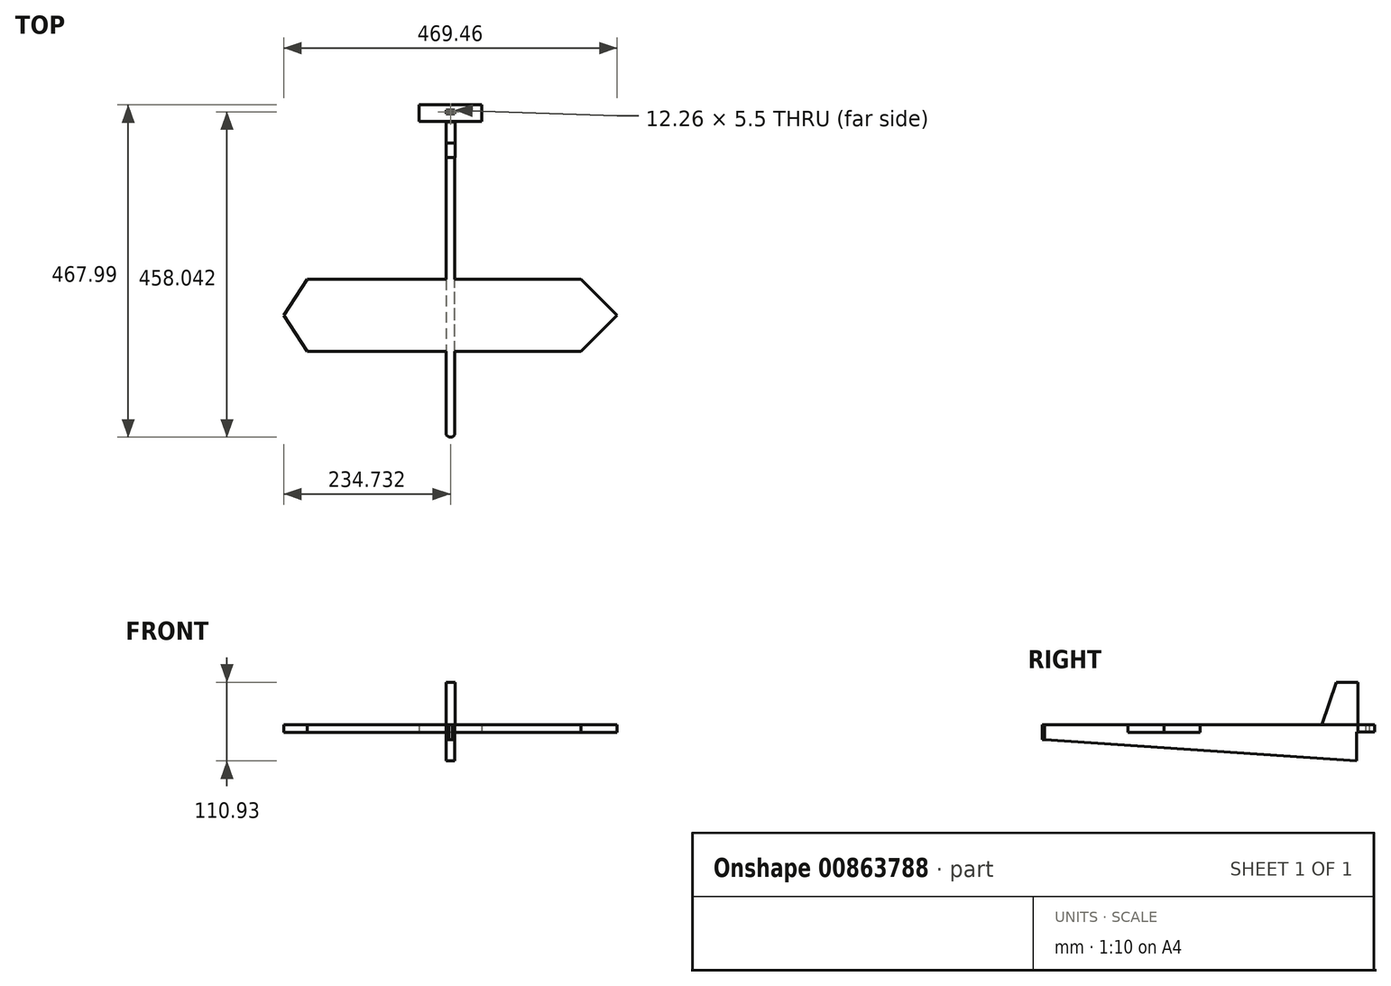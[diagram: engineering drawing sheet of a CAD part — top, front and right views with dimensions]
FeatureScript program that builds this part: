
annotation { "Feature Type Name" : "Feature", "Feature Type Description" : "" }
export const myFeature = defineFeature(function(context is Context, id is Id, definition is map)
    precondition{}
    {
        {
            var Q0;
            Q0=qCreatedBy(makeId("Top.planeOp"),FACE);
            var sketch = newSketch(context, id + "F0", { "sketchPlane" : qUnion([Q0])});
            skLineSegment(sketch, "E0", {"start": v(0, 404.58) * mm, "end": v(0, -52.62) * mm});
            skLineSegment(sketch, "E1", {"start": v(0, -52.62) * mm, "end": v(3.6, -56.2) * mm});
            skLineSegment(sketch, "E2", {"start": v(3.6, -56.2) * mm, "end": v(8.67, -56.2) * mm});
            skLineSegment(sketch, "E3", {"start": v(8.67, -56.2) * mm, "end": v(12.26, -52.62) * mm});
            skLineSegment(sketch, "E4", {"start": v(12.26, -52.62) * mm, "end": v(12.26, 403.42) * mm});
            skLineSegment(sketch, "E5", {"start": v(0, 404.58) * mm, "end": v(12.26, 404.58) * mm});
            skLineSegment(sketch, "E6", {"start": v(12.26, 404.58) * mm, "end": v(12.26, 403.42) * mm});
            skLineSegment(sketch, "E7", {"start": v(12.26, 64.6) * mm, "end": v(240.86, 64.6) * mm});
            skLineSegment(sketch, "E8", {"start": v(240.86, 64.6) * mm, "end": v(240.86, 166.2) * mm});
            skLineSegment(sketch, "E9", {"start": v(240.86, 166.2) * mm, "end": v(12.26, 166.2) * mm});
            skLineSegment(sketch, "E10", {"start": v(12.26, 166.2) * mm, "end": v(0, 166.2) * mm});
            skLineSegment(sketch, "E11", {"start": v(0, 166.2) * mm, "end": v(-228.6, 166.2) * mm});
            skLineSegment(sketch, "E12", {"start": v(-228.6, 166.2) * mm, "end": v(-228.6, 64.6) * mm});
            skLineSegment(sketch, "E13", {"start": v(-228.6, 64.6) * mm, "end": v(12.26, 64.6) * mm});
            skLineSegment(sketch, "E14", {"start": v(12.26, 388.54) * mm, "end": v(37.66, 388.54) * mm});
            skLineSegment(sketch, "E15", {"start": v(37.66, 388.54) * mm, "end": v(12.26, 388.54) * mm});
            skLineSegment(sketch, "E16", {"start": v(0, 388.54) * mm, "end": v(-25.4, 388.54) * mm});
            skLineSegment(sketch, "E17", {"start": v(-25.4, 388.54) * mm, "end": v(-38.1, 388.54) * mm});
            skLineSegment(sketch, "E18", {"start": v(-38.1, 388.54) * mm, "end": v(37.66, 388.54) * mm});
            skLineSegment(sketch, "E19", {"start": v(37.66, 388.54) * mm, "end": v(50.36, 388.54) * mm});
            skLineSegment(sketch, "E20", {"start": v(50.36, 388.54) * mm, "end": v(50.36, 399.08) * mm});
            skLineSegment(sketch, "E21", {"start": v(12.26, 399.08) * mm, "end": v(0, 399.08) * mm});
            skLineSegment(sketch, "E22", {"start": v(-38.1, 399.08) * mm, "end": v(-38.1, 388.54) * mm});
            skLineSegment(sketch, "E23", {"start": v(50.36, 399.08) * mm, "end": v(50.36, 411.78) * mm});
            skLineSegment(sketch, "E24", {"start": v(-38.1, 399.08) * mm, "end": v(-38.1, 411.78) * mm});
            skLineSegment(sketch, "E25", {"start": v(-38.1, 411.78) * mm, "end": v(50.36, 411.78) * mm});
            skSolve(sketch);
        }
        {
            var Q0;
            Q0 = qSketchRegion(id + "F0", true);
            extrude(context, id + "F1", {"entities" : qUnion([Q0]), "depth" : 50.8 * mm, "offsetDistance" : 25.4 * mm});
        }
        {
            var Q0;
            Q0=makeQuery(id+"F1.opExtrude","SWEPT_FACE",FACE,{"disambiguationData":[OSD([sQuery(id+"F0.wireOp",EDGE,"E8")])]});
            var sketch = newSketch(context, id + "F2", { "sketchPlane" : qUnion([Q0])});
            skLineSegment(sketch, "E26", {"start": v(64.6, 40.28) * mm, "end": v(166.2, 40.28) * mm});
            skLineSegment(sketch, "E27", {"start": v(166.2, 40.28) * mm, "end": v(166.2, 50.8) * mm});
            skLineSegment(sketch, "E28", {"start": v(166.2, 50.8) * mm, "end": v(166.2, 40.28) * mm});
            skLineSegment(sketch, "E29", {"start": v(166.2, 40.28) * mm, "end": v(166.2, 0) * mm});
            skLineSegment(sketch, "E30", {"start": v(166.2, 0) * mm, "end": v(64.6, 0) * mm});
            skLineSegment(sketch, "E31", {"start": v(64.6, 0) * mm, "end": v(64.6, 40.28) * mm});
            skSolve(sketch);
        }
        {
            var Q0;
            Q0 = qSketchRegion(id + "F2", true);
            extrude(context, id + "F3", {"entities" : qUnion([Q0]), "operationType" : NewBodyOperationType.REMOVE, "oppositeDirection" : true, "depth" : 228.6 * mm, "offsetDistance" : 25.4 * mm});
        }
        {
            var Q0;
            Q0=makeQuery(id+"F1.opExtrude","SWEPT_FACE",FACE,{"disambiguationData":[OSD([sQuery(id+"F0.wireOp",EDGE,"E12")])]});
            var sketch = newSketch(context, id + "F4", { "sketchPlane" : qUnion([Q0])});
            skLineSegment(sketch, "E32", {"start": v(-166.2, 50.8) * mm, "end": v(-166.2, 40.28) * mm});
            skLineSegment(sketch, "E33", {"start": v(-166.2, 40.28) * mm, "end": v(-64.6, 40.28) * mm});
            skLineSegment(sketch, "E34", {"start": v(-64.6, 40.28) * mm, "end": v(-64.6, 0) * mm});
            skLineSegment(sketch, "E35", {"start": v(-64.6, 0) * mm, "end": v(-166.2, 0) * mm});
            skLineSegment(sketch, "E36", {"start": v(-166.2, 0) * mm, "end": v(-166.42, 40.86) * mm});
            skLineSegment(sketch, "E37", {"start": v(-166.42, 40.86) * mm, "end": v(-64.6, 40.28) * mm});
            skLineSegment(sketch, "E38", {"start": v(-64.6, 0) * mm, "end": v(-64.6, 40.28) * mm});
            skSolve(sketch);
        }
        {
            var Q0;
            Q0 = qSketchRegion(id + "F4", true);
            extrude(context, id + "F5", {"entities" : qUnion([Q0]), "operationType" : NewBodyOperationType.REMOVE, "oppositeDirection" : true, "depth" : 228.6 * mm, "offsetDistance" : 25.4 * mm});
        }
        {
            var Q0;
            {var subQ0=sQuery(id+"F0.wireOp",EDGE,"E0");Q0=makeQuery(id+"FdQB89tJsIS8Kwt_1.boolean.opBoolean","MERGE",FACE,{"derivedFrom":[makeQuery(id+"F1.opExtrude","SWEPT_FACE",FACE,{"disambiguationData":[OSD([subQ0]),TDD([makeQuery(id+"F0.imprint","IMPRINT",EDGE,{"disambiguationData":[TD([[makeQuery(id+"F0.imprint","INTERSECT",VERTEX,{"derivedFrom":[subQ0,sQuery(id+"F0.wireOp",EDGE,"E5")]}),-1.0]])],"derivedFrom":subQ0})])]}),makeQuery(id+"F5.boolean.opBoolean","MERGE",FACE,{"derivedFrom":[makeQuery(id+"F1.opExtrude","SWEPT_FACE",FACE,{"disambiguationData":[OSD([subQ0]),TDD([makeQuery(id+"F0.imprint","IMPRINT",EDGE,{"disambiguationData":[TD([[makeQuery(id+"F0.imprint","INTERSECT",VERTEX,{"derivedFrom":[subQ0,sQuery(id+"F0.wireOp",EDGE,"E18")]}),-1.0]])],"derivedFrom":subQ0})])]}),makeQuery(id+"F1.opExtrude","SWEPT_FACE",FACE,{"disambiguationData":[OSD([subQ0]),TDD([makeQuery(id+"F0.imprint","IMPRINT",EDGE,{"disambiguationData":[TD([[makeQuery(id+"F0.imprint","INTERSECT",VERTEX,{"derivedFrom":[subQ0,sQuery(id+"F0.wireOp",EDGE,"E1")]}),1.0]])],"derivedFrom":subQ0})])]}),makeQuery(id+"F5.opExtrude","CAP_FACE",FACE,{"disambiguationData":[OSD([sQuery(id+"F4.wireOp",EDGE,"E36"),sQuery(id+"F4.wireOp",EDGE,"E37"),sQuery(id+"F4.wireOp",EDGE,"E38"),sQuery(id+"F4.wireOp",EDGE,"E35")])],"isStart":false})]}),makeQuery(id+"FdQB89tJsIS8Kwt_1.opExtrude","SWEPT_FACE",FACE,{"disambiguationData":[OSD([sQuery(id+"FIC4QPpxlJvvk01_1.wireOp",EDGE,"bgQTwSuV-lAzQ-jPFc-NSy7-3OVJcPBx1S6P")])]})]});}
            var sketch = newSketch(context, id + "F6", { "sketchPlane" : qUnion([Q0])});
            skLineSegment(sketch, "E39", {"start": v(865.4, 33.14) * mm, "end": v(404.58, 0) * mm});
            skLineSegment(sketch, "E40", {"start": v(56.47, 0) * mm, "end": v(404.58, 0) * mm});
            skLineSegment(sketch, "E41", {"start": v(56.47, 0) * mm, "end": v(865.4, 33.14) * mm});
            skSolve(sketch);
        }
        {
            var Q0;
            Q0 = qSketchRegion(id + "F6", true);
            extrude(context, id + "F7", {"entities" : qUnion([Q0]), "operationType" : NewBodyOperationType.REMOVE, "oppositeDirection" : true, "depth" : 25.4 * mm, "offsetDistance" : 25.4 * mm});
        }
        {
            var Q0;
            Q0=makeQuery(id+"F1.opExtrude","SWEPT_FACE",FACE,{"disambiguationData":[OSD([sQuery(id+"F0.wireOp",EDGE,"E25")])]});
            var sketch = newSketch(context, id + "F8", { "sketchPlane" : qUnion([Q0])});
            skLineSegment(sketch, "E42", {"start": v(-50.36, 40.75) * mm, "end": v(38.1, 40.75) * mm});
            skLineSegment(sketch, "E43", {"start": v(38.1, 40.75) * mm, "end": v(38.1, 0) * mm});
            skLineSegment(sketch, "E44", {"start": v(38.1, 0) * mm, "end": v(-50.36, 0) * mm});
            skLineSegment(sketch, "E45", {"start": v(-50.36, 0) * mm, "end": v(-50.36, 40.75) * mm});
            skSolve(sketch);
        }
        {
            var Q0;
            Q0 = qSketchRegion(id + "F8", true);
            extrude(context, id + "F9", {"entities" : qUnion([Q0]), "operationType" : NewBodyOperationType.REMOVE, "oppositeDirection" : true, "depth" : 25.4 * mm, "offsetDistance" : 25.4 * mm});
        }
        {
            var Q0;
            {var subQ0=sQuery(id+"F0.wireOp",EDGE,"E0");Q0=makeQuery(id+"F7.boolean.opBoolean","MERGE",FACE,{"derivedFrom":[makeQuery(id+"F5.boolean.opBoolean","MERGE",FACE,{"derivedFrom":[makeQuery(id+"F1.opExtrude","SWEPT_FACE",FACE,{"disambiguationData":[OSD([subQ0]),TDD([makeQuery(id+"F0.imprint","IMPRINT",EDGE,{"disambiguationData":[TD([[makeQuery(id+"F0.imprint","INTERSECT",VERTEX,{"derivedFrom":[subQ0,sQuery(id+"F0.wireOp",EDGE,"E18")]}),-1.0]])],"derivedFrom":subQ0})])]}),makeQuery(id+"F1.opExtrude","SWEPT_FACE",FACE,{"disambiguationData":[OSD([subQ0]),TDD([makeQuery(id+"F0.imprint","IMPRINT",EDGE,{"disambiguationData":[TD([[makeQuery(id+"F0.imprint","INTERSECT",VERTEX,{"derivedFrom":[subQ0,sQuery(id+"F0.wireOp",EDGE,"E1")]}),1.0]])],"derivedFrom":subQ0})])]}),makeQuery(id+"F5.opExtrude","CAP_FACE",FACE,{"disambiguationData":[OSD([sQuery(id+"F4.wireOp",EDGE,"E36"),sQuery(id+"F4.wireOp",EDGE,"E37"),sQuery(id+"F4.wireOp",EDGE,"E38"),sQuery(id+"F4.wireOp",EDGE,"E35")])],"isStart":false})]}),makeQuery(id+"F7.opExtrude","CAP_FACE",FACE,{"disambiguationData":[OSD([sQuery(id+"F6.wireOp",EDGE,"E39"),sQuery(id+"F6.wireOp",EDGE,"E40"),sQuery(id+"F6.wireOp",EDGE,"E41")])],"isStart":true})]});}
            var sketch = newSketch(context, id + "F10", { "sketchPlane" : qUnion([Q0])});
            skLineSegment(sketch, "E46", {"start": v(-309.16, 50.8) * mm, "end": v(-337.9, 50.8) * mm});
            skLineSegment(sketch, "E47", {"start": v(-337.9, 50.8) * mm, "end": v(-358.33, 110.93) * mm});
            skLineSegment(sketch, "E48", {"start": v(-358.33, 110.93) * mm, "end": v(-388.54, 110.93) * mm});
            skLineSegment(sketch, "E49", {"start": v(-388.54, 110.93) * mm, "end": v(-388.54, 50.8) * mm});
            skLineSegment(sketch, "E50", {"start": v(-388.54, 50.8) * mm, "end": v(-388.54, 72.19) * mm});
            skPoint(sketch, "E51.end.orphan", {"position": v(-388.54, 53.46) * mm});
            skLineSegment(sketch, "E52", {"start": v(-388.54, 50.8) * mm, "end": v(-337.9, 50.8) * mm});
            skSolve(sketch);
        }
        {
            var Q0;
            Q0 = qSketchRegion(id + "F10", true);
            extrude(context, id + "F11", {"entities" : qUnion([Q0]), "oppositeDirection" : true, "depth" : 12.7 * mm, "offsetDistance" : 25.4 * mm});
        }
        {
            var Q0;
            {var subQ0=sQuery(id+"F0.wireOp",EDGE,"E4");Q0=makeQuery(id+"F3.boolean.opBoolean","MERGE",FACE,{"derivedFrom":[makeQuery(id+"F1.opExtrude","SWEPT_FACE",FACE,{"disambiguationData":[OSD([subQ0]),TDD([makeQuery(id+"F0.imprint","IMPRINT",EDGE,{"disambiguationData":[TD([[makeQuery(id+"F0.imprint","INTERSECT",VERTEX,{"derivedFrom":[sQuery(id+"F0.wireOp",EDGE,"E3"),subQ0]}),-1.0]])],"derivedFrom":subQ0})])]}),makeQuery(id+"F1.opExtrude","SWEPT_FACE",FACE,{"disambiguationData":[OSD([subQ0]),TDD([makeQuery(id+"F0.imprint","IMPRINT",EDGE,{"disambiguationData":[TD([[makeQuery(id+"F0.imprint","INTERSECT",VERTEX,{"derivedFrom":[subQ0,sQuery(id+"F0.wireOp",EDGE,"E18")]}),1.0]])],"derivedFrom":subQ0})])]}),makeQuery(id+"F3.opExtrude","CAP_FACE",FACE,{"disambiguationData":[OSD([sQuery(id+"F2.wireOp",EDGE,"E26"),sQuery(id+"F2.wireOp",EDGE,"E29"),sQuery(id+"F2.wireOp",EDGE,"E30"),sQuery(id+"F2.wireOp",EDGE,"E31")])],"isStart":false})]});}
            var sketch = newSketch(context, id + "F12", { "sketchPlane" : qUnion([Q0])});
            skLineSegment(sketch, "E53", {"start": v(-56.54, 30.1) * mm, "end": v(386.38, 0) * mm});
            skLineSegment(sketch, "E54", {"start": v(386.38, 0) * mm, "end": v(-56.54, 0) * mm});
            skLineSegment(sketch, "E55", {"start": v(-56.54, 0) * mm, "end": v(-56.54, 30.1) * mm});
            skSolve(sketch);
        }
        {
            var Q0;
            Q0 = qSketchRegion(id + "F12", true);
            extrude(context, id + "F13", {"entities" : qUnion([Q0]), "operationType" : NewBodyOperationType.REMOVE, "oppositeDirection" : true, "depth" : 25.4 * mm, "offsetDistance" : 25.4 * mm});
        }
        {
            var Q0;
            Q0=makeQuery(id+"F1.opExtrude","CAP_FACE",FACE,{"disambiguationData":[OSD([sQuery(id+"F0.wireOp",EDGE,"E0"),sQuery(id+"F0.wireOp",EDGE,"E1"),sQuery(id+"F0.wireOp",EDGE,"E2"),sQuery(id+"F0.wireOp",EDGE,"E3"),sQuery(id+"F0.wireOp",EDGE,"E4"),sQuery(id+"F0.wireOp",EDGE,"E5"),sQuery(id+"F0.wireOp",EDGE,"E6"),sQuery(id+"F0.wireOp",EDGE,"E7"),sQuery(id+"F0.wireOp",EDGE,"E8"),sQuery(id+"F0.wireOp",EDGE,"E9"),sQuery(id+"F0.wireOp",EDGE,"E11"),sQuery(id+"F0.wireOp",EDGE,"E12"),sQuery(id+"F0.wireOp",EDGE,"E13"),sQuery(id+"F0.wireOp",EDGE,"E18"),sQuery(id+"F0.wireOp",EDGE,"E19"),sQuery(id+"F0.wireOp",EDGE,"E20"),sQuery(id+"F0.wireOp",EDGE,"E21"),sQuery(id+"F0.wireOp",EDGE,"E22"),sQuery(id+"F0.wireOp",EDGE,"E23"),sQuery(id+"F0.wireOp",EDGE,"E24"),sQuery(id+"F0.wireOp",EDGE,"E25")])],"isStart":false});
            var sketch = newSketch(context, id + "F14", { "sketchPlane" : qUnion([Q0])});
            skLineSegment(sketch, "E56", {"start": v(0, 166.2) * mm, "end": v(-17.78, 166.2) * mm});
            skLineSegment(sketch, "E57", {"start": v(-17.78, 166.2) * mm, "end": v(-195.58, 166.2) * mm});
            skLineSegment(sketch, "E58", {"start": v(-195.58, 166.2) * mm, "end": v(-228.6, 115.4) * mm});
            skLineSegment(sketch, "E59", {"start": v(0, 64.6) * mm, "end": v(-17.78, 64.6) * mm});
            skLineSegment(sketch, "E60", {"start": v(-17.78, 64.6) * mm, "end": v(-195.58, 64.6) * mm});
            skLineSegment(sketch, "E61", {"start": v(-195.58, 64.6) * mm, "end": v(-228.6, 115.4) * mm});
            skLineSegment(sketch, "E62", {"start": v(-195.58, 166.2) * mm, "end": v(-228.6, 166.2) * mm});
            skLineSegment(sketch, "E63", {"start": v(-228.6, 166.2) * mm, "end": v(-228.6, 64.6) * mm});
            skLineSegment(sketch, "E64", {"start": v(-228.6, 64.6) * mm, "end": v(-195.58, 64.6) * mm});
            skSolve(sketch);
        }
        {
            var Q0;
            Q0 = qSketchRegion(id + "F14", true);
            extrude(context, id + "F15", {"entities" : qUnion([Q0]), "operationType" : NewBodyOperationType.REMOVE, "oppositeDirection" : true, "depth" : 25.4 * mm, "offsetDistance" : 25.4 * mm});
        }
        {
            var Q0;
            Q0=makeQuery(id+"F1.opExtrude","CAP_FACE",FACE,{"disambiguationData":[OSD([sQuery(id+"F0.wireOp",EDGE,"E0"),sQuery(id+"F0.wireOp",EDGE,"E1"),sQuery(id+"F0.wireOp",EDGE,"E2"),sQuery(id+"F0.wireOp",EDGE,"E3"),sQuery(id+"F0.wireOp",EDGE,"E4"),sQuery(id+"F0.wireOp",EDGE,"E5"),sQuery(id+"F0.wireOp",EDGE,"E6"),sQuery(id+"F0.wireOp",EDGE,"E7"),sQuery(id+"F0.wireOp",EDGE,"E8"),sQuery(id+"F0.wireOp",EDGE,"E9"),sQuery(id+"F0.wireOp",EDGE,"E11"),sQuery(id+"F0.wireOp",EDGE,"E12"),sQuery(id+"F0.wireOp",EDGE,"E13"),sQuery(id+"F0.wireOp",EDGE,"E18"),sQuery(id+"F0.wireOp",EDGE,"E19"),sQuery(id+"F0.wireOp",EDGE,"E20"),sQuery(id+"F0.wireOp",EDGE,"E21"),sQuery(id+"F0.wireOp",EDGE,"E22"),sQuery(id+"F0.wireOp",EDGE,"E23"),sQuery(id+"F0.wireOp",EDGE,"E24"),sQuery(id+"F0.wireOp",EDGE,"E25")])],"isStart":false});
            var sketch = newSketch(context, id + "F16", { "sketchPlane" : qUnion([Q0])});
            skLineSegment(sketch, "E65", {"start": v(12.26, 166.2) * mm, "end": v(190.06, 166.2) * mm});
            skLineSegment(sketch, "E66", {"start": v(190.06, 166.2) * mm, "end": v(240.86, 115.4) * mm});
            skLineSegment(sketch, "E67", {"start": v(12.26, 64.6) * mm, "end": v(190.06, 64.6) * mm});
            skLineSegment(sketch, "E68", {"start": v(190.06, 64.6) * mm, "end": v(240.86, 115.4) * mm});
            skLineSegment(sketch, "E69", {"start": v(190.06, 166.2) * mm, "end": v(240.86, 166.2) * mm});
            skLineSegment(sketch, "E70", {"start": v(240.86, 166.2) * mm, "end": v(240.86, 64.6) * mm});
            skLineSegment(sketch, "E71", {"start": v(240.86, 64.6) * mm, "end": v(190.06, 64.6) * mm});
            skSolve(sketch);
        }
        {
            var Q0;
            Q0 = qSketchRegion(id + "F16", true);
            extrude(context, id + "F17", {"entities" : qUnion([Q0]), "operationType" : NewBodyOperationType.REMOVE, "oppositeDirection" : true, "depth" : 25.4 * mm, "offsetDistance" : 25.4 * mm});
        }
    });
